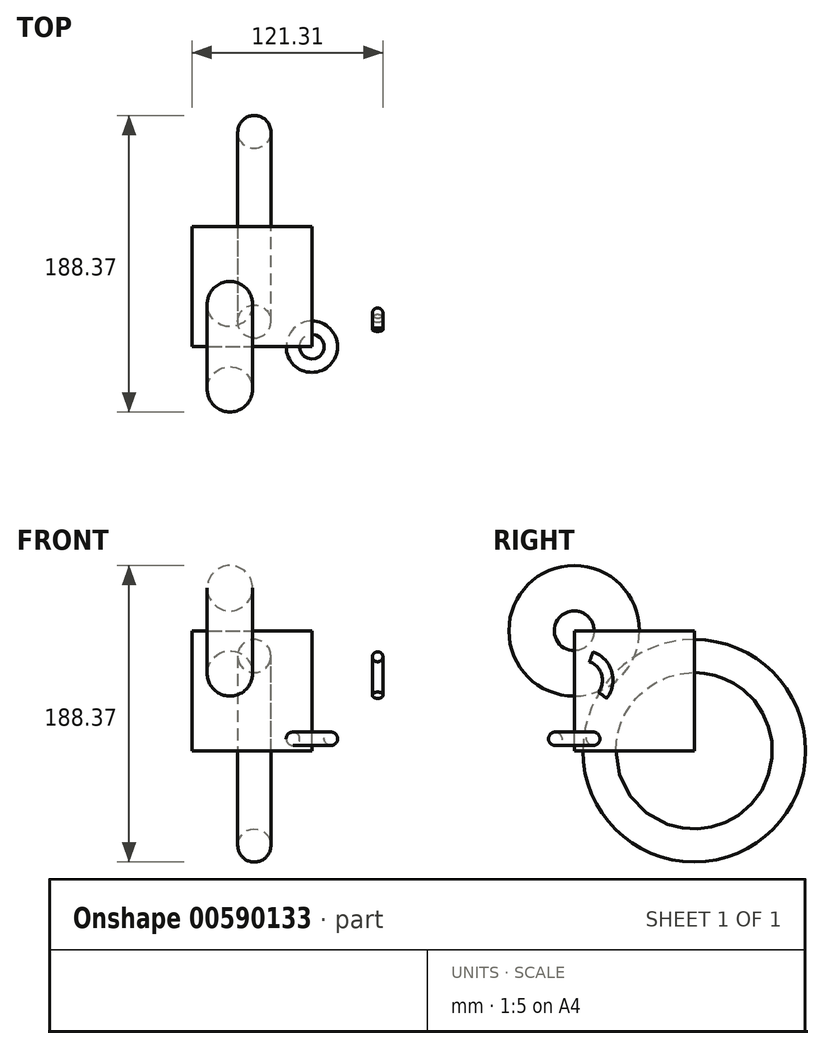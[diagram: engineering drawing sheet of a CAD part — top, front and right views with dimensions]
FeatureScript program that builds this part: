
annotation { "Feature Type Name" : "Feature", "Feature Type Description" : "" }
export const myFeature = defineFeature(function(context is Context, id is Id, definition is map)
    precondition{}
    {
        {
            var Q0;
            Q0=qCreatedBy(makeId("Front.planeOp"),FACE);
            var sketch = newSketch(context, id + "F0", { "sketchPlane" : qUnion([Q0])});
            skLineSegment(sketch, "E0.bottom", {"start": v(0, 0) * mm, "end": v(76.2, 0) * mm});
            skLineSegment(sketch, "E0.top", {"start": v(0, 76.2) * mm, "end": v(76.2, 76.2) * mm});
            skLineSegment(sketch, "E0.left", {"start": v(0, 0) * mm, "end": v(0, 76.2) * mm});
            skLineSegment(sketch, "E0.right", {"start": v(76.2, 0) * mm, "end": v(76.2, 76.2) * mm});
            skSolve(sketch);
        }
        {
            var Q0;
            Q0 = qSketchRegion(id + "F0", true);
            extrude(context, id + "F1", {"entities" : qUnion([Q0]), "depth" : 76.2 * mm, "offsetDistance" : 25.4 * mm});
        }
        {
            var Q0;
            Q0=makeQuery(id+"F1.opExtrude","CAP_FACE",FACE,{"disambiguationData":[OSD([sQuery(id+"F0.wireOp",EDGE,"E0.bottom"),sQuery(id+"F0.wireOp",EDGE,"E0.top"),sQuery(id+"F0.wireOp",EDGE,"E0.left"),sQuery(id+"F0.wireOp",EDGE,"E0.right")])],"isStart":false});
            var sketch = newSketch(context, id + "F2", { "sketchPlane" : qUnion([Q0])});
            skCircle(sketch, "E1", {"center": v(24.12, 49.13) * mm, "radius": 14.4 * mm});
            skSolve(sketch);
        }
        {
            var Q0;
            Q0 = qSketchRegion(id + "F2", true);
            var Q1;
            Q1=makeQuery(id+"F1.opExtrude","CAP_EDGE",EDGE,{"disambiguationData":[OSD([sQuery(id+"F0.wireOp",EDGE,"E0.top")])],"isStart":false});
            revolve(context, id + "F3", {"entities" : qUnion([Q0]), "axis" : qUnion([Q1]), "revolveType" : RevolveType.FULL});
        }
        {
            var Q0;
            Q0=makeQuery(id+"F1.opExtrude","CAP_FACE",FACE,{"disambiguationData":[OSD([sQuery(id+"F0.wireOp",EDGE,"E0.bottom"),sQuery(id+"F0.wireOp",EDGE,"E0.top"),sQuery(id+"F0.wireOp",EDGE,"E0.left"),sQuery(id+"F0.wireOp",EDGE,"E0.right")])],"isStart":true});
            var sketch = newSketch(context, id + "F4", { "sketchPlane" : qUnion([Q0])});
            skCircle(sketch, "E2", {"center": v(-39.62, 60.17) * mm, "radius": 10.51 * mm});
            skSolve(sketch);
        }
        {
            var Q0;
            Q0 = qSketchRegion(id + "F4", true);
            var Q1;
            Q1=makeQuery(id+"F1.opExtrude","CAP_EDGE",EDGE,{"disambiguationData":[OSD([sQuery(id+"F0.wireOp",EDGE,"E0.bottom")])],"isStart":true});
            revolve(context, id + "F5", {"entities" : qUnion([Q0]), "axis" : qUnion([Q1]), "revolveType" : RevolveType.FULL});
        }
        {
            var Q0;
            Q0=makeQuery(id+"F1.opExtrude","SWEPT_FACE",FACE,{"disambiguationData":[OSD([sQuery(id+"F0.wireOp",EDGE,"E0.right")])]});
            var sketch = newSketch(context, id + "F6", { "sketchPlane" : qUnion([Q0])});
            skCircle(sketch, "E3.cCircle", {"center": v(-52.53, 50.18) * mm, "radius": 15.26 * mm, "construction": true});
            skLineSegment(sketch, "E3.0", {"start": v(-34.77, 43.81) * mm, "end": v(-53.1, 31.33) * mm});
            skLineSegment(sketch, "E3.1", {"start": v(-53.1, 31.33) * mm, "end": v(-70.64, 44.9) * mm});
            skLineSegment(sketch, "E3.2", {"start": v(-70.64, 44.9) * mm, "end": v(-63.16, 65.78) * mm});
            skLineSegment(sketch, "E3.3", {"start": v(-63.16, 65.78) * mm, "end": v(-40.99, 65.1) * mm});
            skLineSegment(sketch, "E3.4", {"start": v(-40.99, 65.1) * mm, "end": v(-34.77, 43.81) * mm});
            skPoint(sketch, "E3.0.midPoint", {"position": v(-43.94, 37.57) * mm});
            skSolve(sketch);
        }
        {
            var Q0;
            Q0 = qSketchRegion(id + "F6", true);
            var Q1;
            Q1=makeQuery(id+"F1.opExtrude","SWEPT_FACE",FACE,{"disambiguationData":[OSD([sQuery(id+"F0.wireOp",EDGE,"E0.left")])]});
            extrude(context, id + "F7", {"entities" : qUnion([Q0]), "depth" : 51.05 * mm, "endBoundEntityFace" : qUnion([Q1]), "offsetDistance" : 25.4 * mm});
        }
        {
            var Q0;
            Q0=makeQuery(id+"F1.opExtrude","SWEPT_FACE",FACE,{"disambiguationData":[OSD([sQuery(id+"F0.wireOp",EDGE,"E0.top")])]});
            var sketch = newSketch(context, id + "F8", { "sketchPlane" : qUnion([Q0])});
            skCircle(sketch, "E4", {"center": v(47.8, -25.06) * mm, "radius": 15.14 * mm});
            skSolve(sketch);
        }
        {
            var Q0;
            Q0 = qSketchRegion(id + "F8", true);
            var Q1;
            Q1=makeQuery(id+"F1.opExtrude","SWEPT_EDGE",EDGE,{"disambiguationData":[OSD([sQuery(id+"F0.wireOp",EDGE,"E0.top"),sQuery(id+"F0.wireOp",EDGE,"E0.right")])]});
            revolve(context, id + "F9", {"entities" : qUnion([Q0]), "axis" : qUnion([Q1]), "revolveType" : RevolveType.FULL});
        }
        {
            var Q0;
            Q0=makeQuery(id+"F9.opRevolve","SWEPT_BODY",BODY,{"disambiguationData":[OSD([sQuery(id+"F8.wireOp",EDGE,"E4")])]});
            var Q1;
            Q1=makeQuery(id+"F3.opRevolve","SWEPT_BODY",BODY,{"disambiguationData":[OSD([sQuery(id+"F2.wireOp",EDGE,"E1")])]});
            booleanBodies(context, id + "F10", {"operationType" : BooleanOperationType.SUBTRACTION, "tools" : qUnion([Q0]), "targets" : qUnion([Q1])});
        }
        {
            var Q0;
            Q0=makeQuery(id+"F3.opRevolve","SWEPT_BODY",BODY,{"disambiguationData":[OSD([sQuery(id+"F2.wireOp",EDGE,"E1")])]});
            var Q1;
            Q1=makeQuery(id+"F5.opRevolve","SWEPT_BODY",BODY,{"disambiguationData":[OSD([sQuery(id+"F4.wireOp",EDGE,"E2")])]});
            booleanBodies(context, id + "F11", {"operationType" : BooleanOperationType.INTERSECTION, "tools" : qUnion([Q0, Q1]), "keepTools" : true});
        }
        {
            var Q0;
            Q0=makeQuery(id+"F1.opExtrude","CAP_FACE",FACE,{"disambiguationData":[OSD([sQuery(id+"F0.wireOp",EDGE,"E0.bottom"),sQuery(id+"F0.wireOp",EDGE,"E0.top"),sQuery(id+"F0.wireOp",EDGE,"E0.left"),sQuery(id+"F0.wireOp",EDGE,"E0.right")])],"isStart":false});
            var sketch = newSketch(context, id + "F12", { "sketchPlane" : qUnion([Q0])});
            skCircle(sketch, "E5", {"center": v(64.14, 7.62) * mm, "radius": 4.26 * mm});
            skSolve(sketch);
        }
        {
            var Q0;
            Q0 = qSketchRegion(id + "F12", true);
            var Q1;
            Q1=makeQuery(id+"F1.opExtrude","CAP_EDGE",EDGE,{"disambiguationData":[OSD([sQuery(id+"F0.wireOp",EDGE,"E0.right")])],"isStart":false});
            revolve(context, id + "F13", {"entities" : qUnion([Q0]), "axis" : qUnion([Q1]), "revolveType" : RevolveType.FULL});
        }
        {
            var Q0;
            Q0=makeQuery(id+"F7.opExtrude","SWEPT_FACE",FACE,{"disambiguationData":[OSD([sQuery(id+"F6.wireOp",EDGE,"E3.1")])]});
            var sketch = newSketch(context, id + "F14", { "sketchPlane" : qUnion([Q0])});
            skCircle(sketch, "E6", {"center": v(117.96, 67.64) * mm, "radius": 3.35 * mm});
            skSolve(sketch);
        }
        {
            var Q0;
            Q0 = qSketchRegion(id + "F14", true);
            var Q1;
            Q1=makeQuery(id+"F7.opExtrude","SWEPT_EDGE",EDGE,{"disambiguationData":[OSD([sQuery(id+"F6.wireOp",EDGE,"E3.1"),sQuery(id+"F6.wireOp",EDGE,"E3.2")])]});
            revolve(context, id + "F15", {"entities" : qUnion([Q0]), "axis" : qUnion([Q1]), "revolveType" : RevolveType.FULL});
        }
        {
            var Q0;
            Q0=makeQuery(id+"F7.opExtrude","SWEPT_BODY",BODY,{"disambiguationData":[OSD([sQuery(id+"F6.wireOp",EDGE,"E3.0"),sQuery(id+"F6.wireOp",EDGE,"E3.1"),sQuery(id+"F6.wireOp",EDGE,"E3.2"),sQuery(id+"F6.wireOp",EDGE,"E3.3"),sQuery(id+"F6.wireOp",EDGE,"E3.4")])]});
            var Q1;
            Q1=makeQuery(id+"F15.opRevolve","SWEPT_BODY",BODY,{"disambiguationData":[OSD([sQuery(id+"F14.wireOp",EDGE,"E6")])]});
            booleanBodies(context, id + "F16", {"operationType" : BooleanOperationType.INTERSECTION, "tools" : qUnion([Q0, Q1])});
        }
    });
